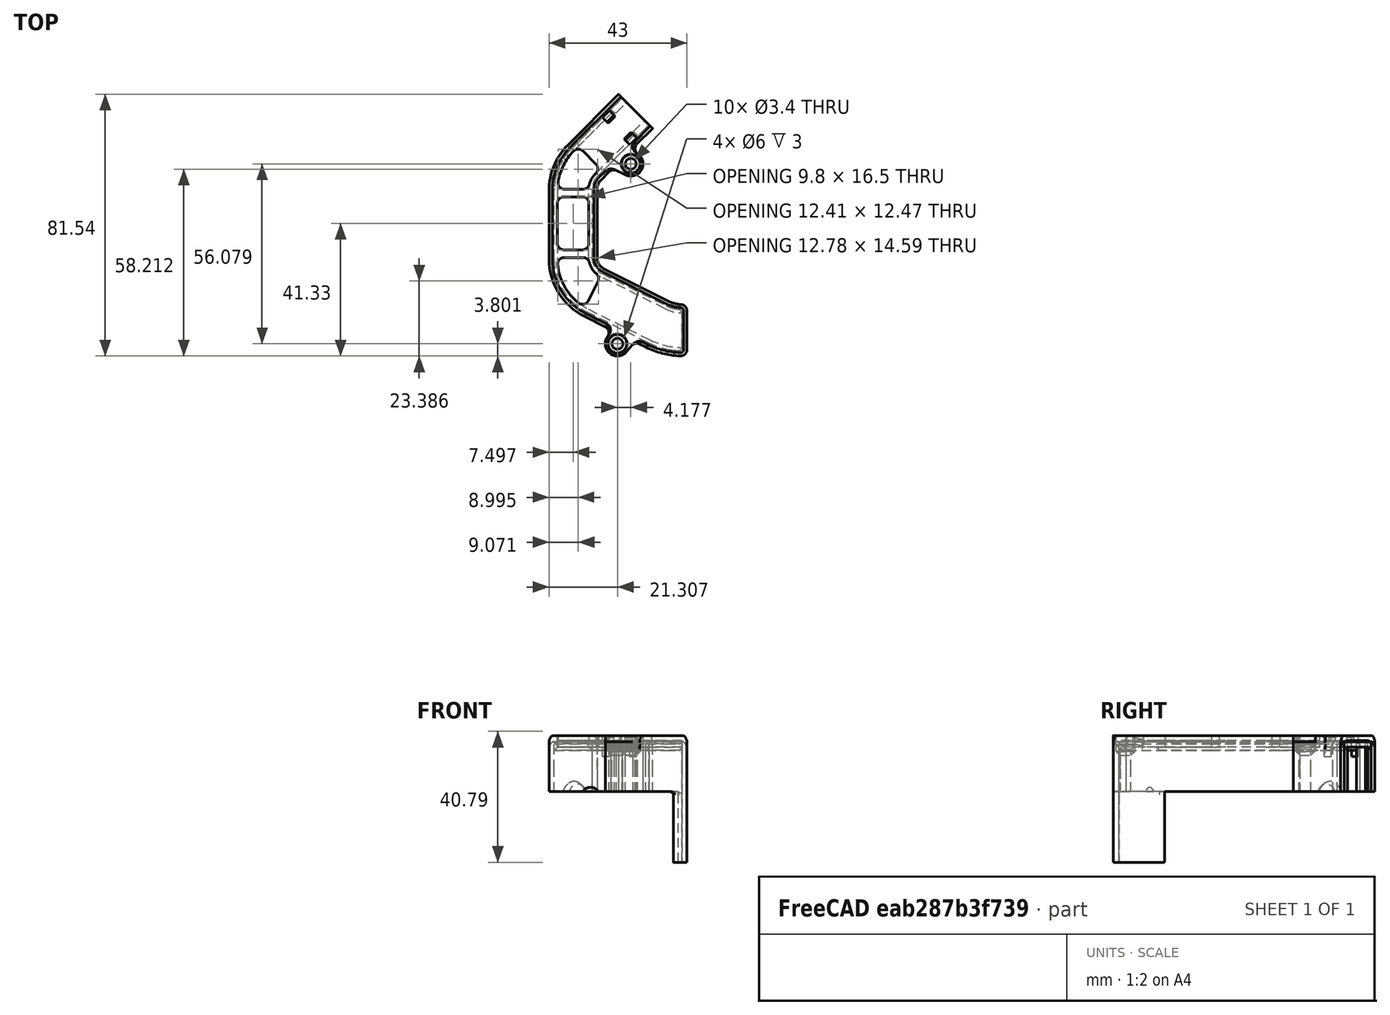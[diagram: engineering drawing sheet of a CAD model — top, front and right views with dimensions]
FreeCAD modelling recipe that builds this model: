
FCSTD DOCUMENT  (FreeCAD 0.18R16146 (Git))
Label: back-cable-cover
License: Other
LicenseURL: GPL3
objects: Part::MultiFuse×5, Part::Feature×4, Part::Cylinder×4, Part::MultiCommon×4, Part::Box×4, Part::Chamfer×2, Part::Cut×1
note: 24 computed .brp shape members not serialized (recipe doc carries the construction recipe); baked Part::Feature solids carry a one-line shape summary decoded from their .brp

FEATURE [Part::Feature] Part__Feature198  label="cable cover"
  Placement = pos=(349.507,-268.023,-59.004) rot=(0,0,1;1.5708rad)
  shape: bbox 44.65 x 83.66 x 35.3 mm, 157 faces (baked)
FEATURE [Part::Cylinder] Cylinder
  Angle = 360
  AttacherType = Attacher::AttachEngine3D
  Height = 53
  Placement = pos=(0,0,-46) rot=(0,0,1;0rad)
  Radius = 48
FEATURE [Part::Cylinder] Cylinder001
  Angle = 360
  AttacherType = Attacher::AttachEngine3D
  Height = 26
  Placement = pos=(0,0,3.5) rot=(0,0,1;0rad)
  Radius = 48
FEATURE [Part::Feature] Part__Feature199  label="cable cover001"
  Placement = pos=(349.507,-268.023,-59.004) rot=(0,0,1;1.5708rad)
  shape: bbox 44.65 x 83.66 x 35.3 mm, 157 faces (baked)
FEATURE [Part::MultiCommon] Common
  Shapes = -> [Part__Feature199,Cylinder]
FEATURE [Part::MultiCommon] Common001
  Placement = pos=(0,0,3.5) rot=(0,0,1;0rad)
  Shapes = -> [Cylinder001,Part__Feature198]
FEATURE [Part::MultiFuse] Fusion
  Shapes = -> [Common001,Common]
FEATURE [Part::Box] Box  label="Cube"
  AttacherType = Attacher::AttachEngine3D
  Height = 14
  Length = 2
  Placement = pos=(6.71751,36.1619,0) rot=(0,0,1;5.49779rad)
  Width = 5
FEATURE [Part::Box] Box001  label="Cube001"
  AttacherType = Attacher::AttachEngine3D
  Height = 14
  Length = 2
  Placement = pos=(-0.282843,43.1622,0) rot=(0,0,-1;0.785398rad)
  Width = 5
FEATURE [Part::MultiFuse] Fusion001
  Shapes = -> [Box001,Box]
FEATURE [Part::Chamfer] Chamfer
  Base = -> Fusion001
  Edges = 3 edges r=0.5: [Edge5,Edge7,Edge15]
FEATURE [Part::Cylinder] Cylinder002
  Angle = 360
  AttacherType = Attacher::AttachEngine3D
  Height = 53
  Placement = pos=(0,0,-46) rot=(0,0,1;0rad)
  Radius = 48
FEATURE [Part::Cylinder] Cylinder003
  Angle = 360
  AttacherType = Attacher::AttachEngine3D
  Height = 26
  Placement = pos=(0,0,3.5) rot=(0,0,1;0rad)
  Radius = 48
FEATURE [Part::MultiFuse] Fusion002
  Shapes = -> [Fusion,Chamfer]
FEATURE [Part::Feature] Fusion002001  label="Fusion003"
  shape: bbox 44.65 x 83.66 x 38.8 mm, 171 faces (baked)
FEATURE [Part::Feature] Fusion002002  label="Fusion004"
  shape: bbox 44.65 x 83.66 x 38.8 mm, 171 faces (baked)
FEATURE [Part::MultiCommon] Common002
  Placement = pos=(0,0,2) rot=(0,0,1;0rad)
  Shapes = -> [Cylinder003,Fusion002002]
FEATURE [Part::MultiCommon] Common003
  Shapes = -> [Fusion002001,Cylinder002]
FEATURE [Part::MultiFuse] Fusion002003
  Shapes = -> [Common002,Common003]
FEATURE [Part::Box] Box002  label="Cube002"
  AttacherType = Attacher::AttachEngine3D
  Height = 10
  Length = 2
  Placement = pos=(4.24264,33.5355,0) rot=(0,0,1;5.49779rad)
  Width = 3
FEATURE [Part::Box] Box003  label="Cube003"
  AttacherType = Attacher::AttachEngine3D
  Height = 10
  Length = 2
  Placement = pos=(-2.82843,40.6066,0) rot=(0,0,-1;0.785398rad)
  Width = 3
FEATURE [Part::MultiFuse] Fusion002004
  Placement = pos=(0,0,11) rot=(0,0,1;0rad)
  Shapes = -> [Box003,Box002]
FEATURE [Part::Cut] Cut
  Base = -> Fusion002003
  Tool = -> Fusion002004
FEATURE [Part::Chamfer] Chamfer001
  Base = -> Cut
  Edges = 2 edges r=0.5: [Edge100,Edge128]
